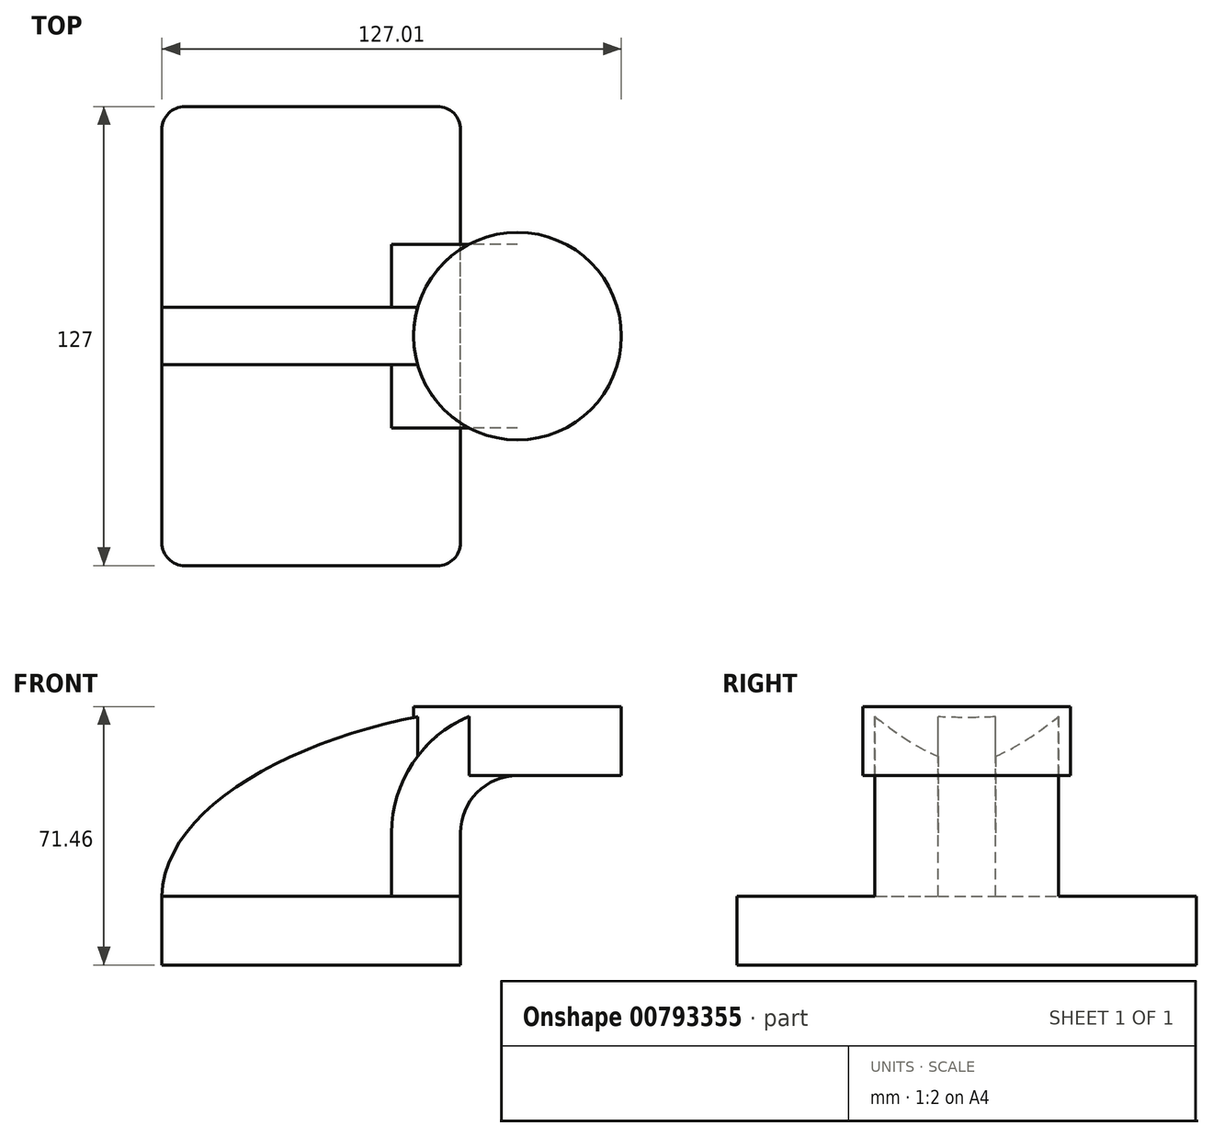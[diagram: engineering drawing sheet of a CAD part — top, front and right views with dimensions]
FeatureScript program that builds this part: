
annotation { "Feature Type Name" : "Feature", "Feature Type Description" : "" }
export const myFeature = defineFeature(function(context is Context, id is Id, definition is map)
    precondition{}
    {
        {
            var Q0;
            Q0=qCreatedBy(makeId("Front.planeOp"),FACE);
            var sketch = newSketch(context, id + "F0", { "sketchPlane" : qUnion([Q0])});
            skLineSegment(sketch, "E0.bottom", {"start": v(41.27, 9.53) * mm, "end": v(-41.28, 9.53) * mm});
            skLineSegment(sketch, "E0.top", {"start": v(41.28, -9.52) * mm, "end": v(-41.27, -9.52) * mm});
            skLineSegment(sketch, "E0.left", {"start": v(41.28, 9.53) * mm, "end": v(41.28, -9.52) * mm});
            skLineSegment(sketch, "E0.right", {"start": v(-41.28, 9.53) * mm, "end": v(-41.27, -9.52) * mm});
            skPoint(sketch, "E0.middle", {"position": v(0, 0) * mm});
            skLineSegment(sketch, "E1.bottom", {"start": v(107.82, 66.68) * mm, "end": v(57.02, 66.68) * mm});
            skLineSegment(sketch, "E1.top", {"start": v(107.82, 38.1) * mm, "end": v(57.02, 38.1) * mm});
            skLineSegment(sketch, "E1.left", {"start": v(107.82, 66.68) * mm, "end": v(107.82, 38.1) * mm});
            skLineSegment(sketch, "E1.right", {"start": v(57.02, 66.68) * mm, "end": v(57.02, 38.1) * mm});
            skPoint(sketch, "E1.middle", {"position": v(82.42, 52.39) * mm});
            skLineSegment(sketch, "E2", {"start": v(41.27, 9.53) * mm, "end": v(41.27, 27) * mm});
            skArc(sketch, "E3", {"start": v(41.27, 27) * mm, "mid": v(45.92, 38.23) * mm, "end": v(57.15, 42.88) * mm});
            skLineSegment(sketch, "E4", {"start": v(57.15, 42.88) * mm, "end": v(85.73, 42.88) * mm});
            skLineSegment(sketch, "E5.0", {"start": v(57.15, 61.93) * mm, "end": v(85.73, 61.93) * mm});
            skArc(sketch, "E5.1", {"start": v(22.23, 27) * mm, "mid": v(32.45, 51.7) * mm, "end": v(57.15, 61.93) * mm});
            skLineSegment(sketch, "E5.2", {"start": v(22.23, 9.53) * mm, "end": v(22.23, 27) * mm});
            skLineSegment(sketch, "E6", {"start": v(85.73, 61.93) * mm, "end": v(85.73, 42.88) * mm});
            skFitSpline(sketch, "E7", {"points": [v(-41.28, 9.53) * mm, v(57.15, 61.93) * mm], "startDerivative": vector(2.15, 91.3) * mm, "endDerivative": vector(128.3, 0.41) * mm});
            skSolve(sketch);
        }
        {
            var Q0;
            Q0=makeQuery(id+"F0.imprint","IMPRINT",FACE,{"disambiguationData":[TD([[makeQuery(id+"F0.imprint","IMPRINT",EDGE,{"derivedFrom":sQuery(id+"F0.wireOp",EDGE,"E0.top")}),-1.0]])]});
            extrude(context, id + "F1", {"entities" : qUnion([Q0]), "endBound" : BoundingType.SYMMETRIC, "depth" : 127 * mm, "offsetDistance" : 25.4 * mm});
        }
        {
            var Q0;
            {var subQ1=sQuery(id+"F0.wireOp",EDGE,"E2");Q0=makeQuery(id+"F0.imprint","IMPRINT",FACE,{"disambiguationData":[TD([[makeQuery(id+"F0.imprint","IMPRINT",EDGE,{"derivedFrom":subQ1}),1.0]])]});}
            extrude(context, id + "F2", {"entities" : qUnion([Q0]), "operationType" : NewBodyOperationType.ADD, "endBound" : BoundingType.SYMMETRIC, "depth" : 50.8 * mm, "offsetDistance" : 25.4 * mm});
        }
        {
            var Q0;
            {var subQ3=sQuery(id+"F0.wireOp",EDGE,"E5.2");Q0=makeQuery(id+"F0.imprint","IMPRINT",FACE,{"disambiguationData":[TD([[makeQuery(id+"F0.imprint","IMPRINT",EDGE,{"derivedFrom":subQ3}),1.0]])]});}
            extrude(context, id + "F3", {"entities" : qUnion([Q0]), "operationType" : NewBodyOperationType.ADD, "endBound" : BoundingType.SYMMETRIC, "depth" : 15.88 * mm, "offsetDistance" : 25.4 * mm});
        }
        {
            var Q0;
            {var subQ1=sQuery(id+"F0.wireOp",EDGE,"E4");Q0=makeQuery(id+"F0.imprint","IMPRINT",FACE,{"disambiguationData":[TD([[makeQuery(id+"F0.imprint","IMPRINT",EDGE,{"derivedFrom":subQ1}),1.0]])]});}
            var Q1;
            Q1=sQuery(id+"F0.wireOp",EDGE,"E1.right");
            revolve(context, id + "F4", {"operationType" : NewBodyOperationType.ADD, "surfaceOperationType" : NewSurfaceOperationType.NEW, "entities" : qUnion([Q0]), "axis" : qUnion([Q1]), "revolveType" : RevolveType.FULL});
        }
        {
            var Q0;
            Q0=makeQuery(id+"F1.opExtrude","CAP_EDGE",EDGE,{"disambiguationData":[OSD([sQuery(id+"F0.wireOp",EDGE,"E0.left")])],"isStart":false});
            var Q1;
            Q1=makeQuery(id+"F1.opExtrude","CAP_EDGE",EDGE,{"disambiguationData":[OSD([sQuery(id+"F0.wireOp",EDGE,"E0.right")])],"isStart":false});
            var Q2;
            Q2=makeQuery(id+"F1.opExtrude","CAP_EDGE",EDGE,{"disambiguationData":[OSD([sQuery(id+"F0.wireOp",EDGE,"E0.left")])],"isStart":true});
            var Q3;
            Q3=makeQuery(id+"F1.opExtrude","CAP_EDGE",EDGE,{"disambiguationData":[OSD([sQuery(id+"F0.wireOp",EDGE,"E0.right")])],"isStart":true});
            fillet(context, id + "F5", {"entities" : qUnion([Q0, Q1, Q2, Q3]), "radius" : 6.35 * mm, "tangentPropagation" : true, "allowEdgeOverflow" : false});
        }
    });
